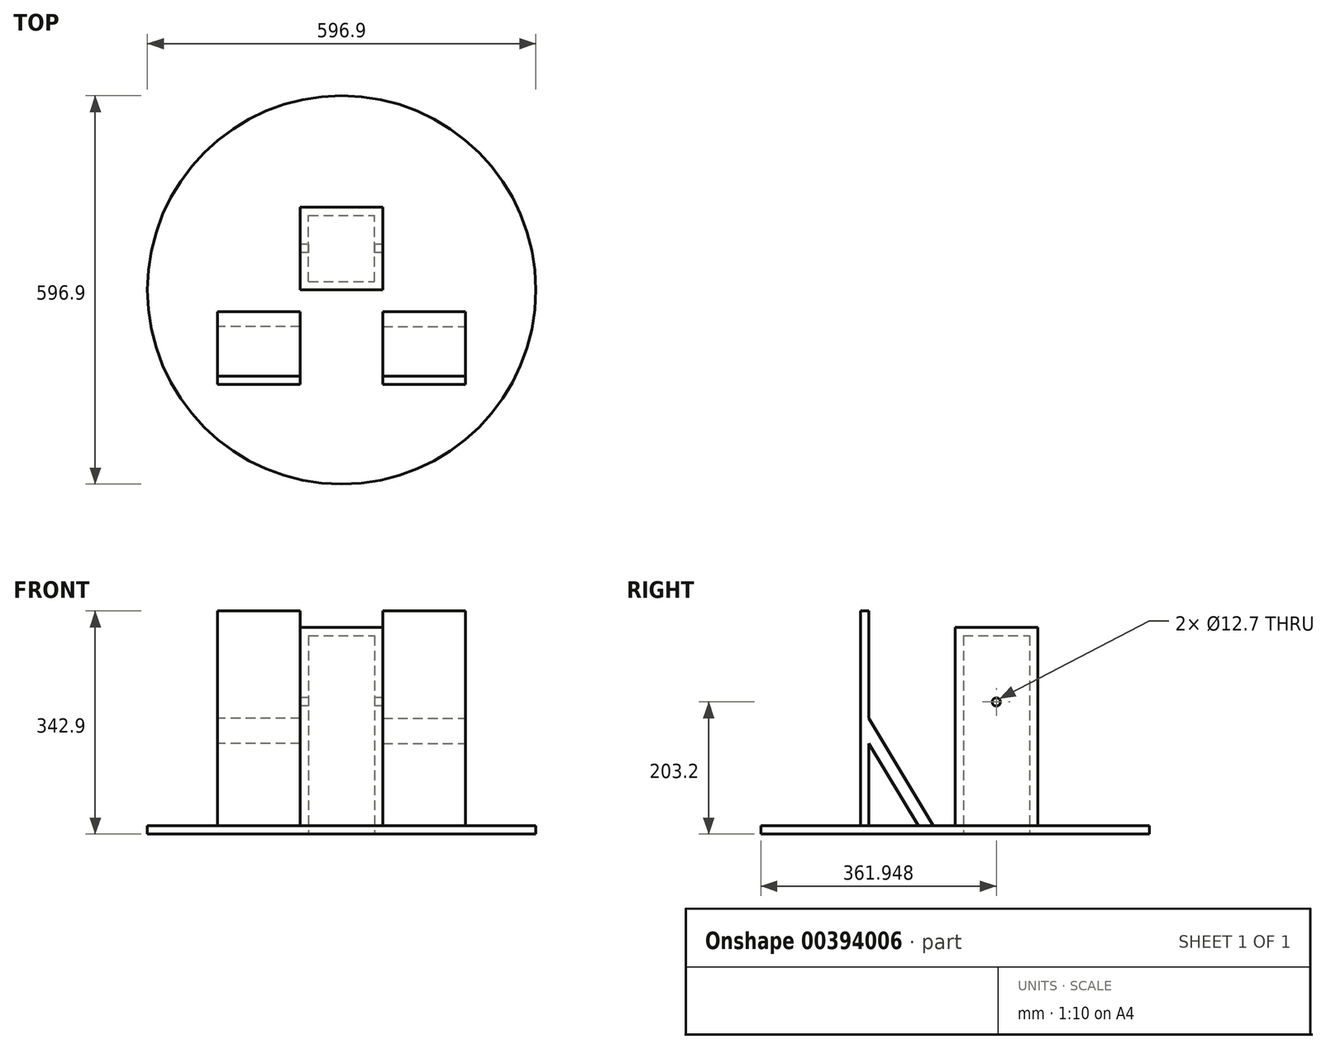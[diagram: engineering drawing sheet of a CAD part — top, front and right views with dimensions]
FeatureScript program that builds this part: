
annotation { "Feature Type Name" : "Feature", "Feature Type Description" : "" }
export const myFeature = defineFeature(function(context is Context, id is Id, definition is map)
    precondition{}
    {
        {
            var Q0;
            Q0=qCreatedBy(makeId("Top.planeOp"),FACE);
            var sketch = newSketch(context, id + "F0", { "sketchPlane" : qUnion([Q0])});
            skLineSegment(sketch, "E0.bottom", {"start": v(-59.76, 60.85) * mm, "end": v(67.24, 60.85) * mm});
            skLineSegment(sketch, "E0.top", {"start": v(-59.76, -66.15) * mm, "end": v(67.24, -66.15) * mm});
            skLineSegment(sketch, "E0.left", {"start": v(-59.76, 60.85) * mm, "end": v(-59.76, -66.15) * mm});
            skLineSegment(sketch, "E0.right", {"start": v(67.24, 60.85) * mm, "end": v(67.24, -66.15) * mm});
            skSolve(sketch);
        }
        {
            var Q0;
            Q0=qSketchRegion(id+"F0",true);
            extrude(context, id + "F1", {"entities" : qUnion([Q0]), "depth" : 304.8 * mm});
        }
        {
            var Q0;
            Q0=makeQuery(id+"F1.opExtrude","CAP_FACE",FACE,{"disambiguationData":[OSD([sQuery(id+"F0.wireOp",EDGE,"E0.bottom"),sQuery(id+"F0.wireOp",EDGE,"E0.top"),sQuery(id+"F0.wireOp",EDGE,"E0.left"),sQuery(id+"F0.wireOp",EDGE,"E0.right")])],"isStart":true});
            var sketch = newSketch(context, id + "F2", { "sketchPlane" : qUnion([Q0])});
            skLineSegment(sketch, "E1.0", {"start": v(-47.06, -60.85) * mm, "end": v(-47.06, 66.15) * mm, "construction": true});
            skLineSegment(sketch, "E2.0", {"start": v(-59.76, 53.45) * mm, "end": v(67.24, 53.45) * mm, "construction": true});
            skLineSegment(sketch, "E3.0", {"start": v(54.54, -60.85) * mm, "end": v(54.54, 66.15) * mm, "construction": true});
            skLineSegment(sketch, "E4.0", {"start": v(-59.76, -48.15) * mm, "end": v(67.24, -48.15) * mm, "construction": true});
            skLineSegment(sketch, "E5.bottom", {"start": v(-47.06, 53.45) * mm, "end": v(54.54, 53.45) * mm});
            skLineSegment(sketch, "E5.top", {"start": v(-47.06, -48.15) * mm, "end": v(54.54, -48.15) * mm});
            skLineSegment(sketch, "E5.left", {"start": v(-47.06, 53.45) * mm, "end": v(-47.06, -48.15) * mm});
            skLineSegment(sketch, "E5.right", {"start": v(54.54, 53.45) * mm, "end": v(54.54, -48.15) * mm});
            skSolve(sketch);
        }
        {
            var Q0;
            Q0=qSketchRegion(id+"F2",true);
            extrude(context, id + "F3", {"entities" : qUnion([Q0]), "operationType" : NewBodyOperationType.REMOVE, "oppositeDirection" : true, "depth" : 292.1 * mm});
        }
        {
            var Q0;
            Q0=makeQuery(id+"F1.opExtrude","SWEPT_FACE",FACE,{"disambiguationData":[OSD([sQuery(id+"F0.wireOp",EDGE,"E0.left")])]});
            var sketch = newSketch(context, id + "F4", { "sketchPlane" : qUnion([Q0])});
            skLineSegment(sketch, "E6.0", {"start": v(-60.85, 190.5) * mm, "end": v(66.15, 190.5) * mm, "construction": true});
            skCircle(sketch, "E7", {"center": v(2.65, 190.5) * mm, "radius": 6.35 * mm});
            skSolve(sketch);
        }
        {
            var Q0;
            Q0=qSketchRegion(id+"F4",true);
            extrude(context, id + "F5", {"entities" : qUnion([Q0]), "operationType" : NewBodyOperationType.REMOVE, "endBound" : BoundingType.THROUGH_ALL, "oppositeDirection" : true, "depth" : 25.4 * mm});
        }
        {
            var Q0;
            Q0=makeQuery(id+"F1.opExtrude","CAP_FACE",FACE,{"disambiguationData":[OSD([sQuery(id+"F0.wireOp",EDGE,"E0.bottom"),sQuery(id+"F0.wireOp",EDGE,"E0.top"),sQuery(id+"F0.wireOp",EDGE,"E0.left"),sQuery(id+"F0.wireOp",EDGE,"E0.right")])],"isStart":true});
            var sketch = newSketch(context, id + "F6", { "sketchPlane" : qUnion([Q0])});
            skCircle(sketch, "E8", {"center": v(3.74, 66.15) * mm, "radius": 298.45 * mm});
            skLineSegment(sketch, "E9", {"start": v(-47.06, 53.45) * mm, "end": v(-47.06, -48.15) * mm});
            skLineSegment(sketch, "E10", {"start": v(-47.06, -48.15) * mm, "end": v(54.54, -48.15) * mm});
            skLineSegment(sketch, "E11", {"start": v(54.54, -48.15) * mm, "end": v(54.54, 53.45) * mm});
            skLineSegment(sketch, "E12", {"start": v(54.54, 53.45) * mm, "end": v(-47.06, 53.45) * mm});
            skLineSegment(sketch, "E13", {"start": v(3.74, 66.15) * mm, "end": v(-294.7, 66.15) * mm});
            skLineSegment(sketch, "E14", {"start": v(3.74, 66.15) * mm, "end": v(302.2, 66.15) * mm});
            skSolve(sketch);
        }
        {
            var Q0;
            Q0=qSketchRegion(id+"F6",true);
            extrude(context, id + "F7", {"entities" : qUnion([Q0]), "operationType" : NewBodyOperationType.ADD, "depth" : 12.7 * mm});
        }
        {
            var Q0;
            Q0=makeQuery(id+"F7.opExtrude","CAP_FACE",FACE,{"disambiguationData":[OSD([sQuery(id+"F6.wireOp",EDGE,"E8"),sQuery(id+"F6.wireOp",EDGE,"E9"),sQuery(id+"F6.wireOp",EDGE,"E10"),sQuery(id+"F6.wireOp",EDGE,"E11"),sQuery(id+"F6.wireOp",EDGE,"E12")])],"isStart":true});
            var sketch = newSketch(context, id + "F8", { "sketchPlane" : qUnion([Q0])});
            skLineSegment(sketch, "E15.bottom", {"start": v(-59.76, -211.2) * mm, "end": v(-186.76, -211.2) * mm});
            skLineSegment(sketch, "E15.top", {"start": v(-59.76, -198.5) * mm, "end": v(-186.76, -198.5) * mm});
            skLineSegment(sketch, "E15.left", {"start": v(-59.76, -211.2) * mm, "end": v(-59.76, -198.5) * mm});
            skLineSegment(sketch, "E15.right", {"start": v(-186.76, -211.2) * mm, "end": v(-186.76, -198.5) * mm});
            skLineSegment(sketch, "E16.MirrorCS", {"start": v(67.24, -198.5) * mm, "end": v(194.24, -198.5) * mm});
            skLineSegment(sketch, "E17.MirrorCS", {"start": v(67.24, -211.2) * mm, "end": v(67.24, -198.5) * mm});
            skLineSegment(sketch, "E18.MirrorCS", {"start": v(194.24, -211.2) * mm, "end": v(194.24, -198.5) * mm});
            skLineSegment(sketch, "E19.MirrorCS", {"start": v(67.24, -211.2) * mm, "end": v(194.24, -211.2) * mm});
            skPoint(sketch, "E20.start.orphan", {"position": v(3.74, -66.15) * mm});
            skSolve(sketch);
        }
        {
            var Q0;
            Q0=qSketchRegion(id+"F8",true);
            extrude(context, id + "F9", {"entities" : qUnion([Q0]), "operationType" : NewBodyOperationType.ADD, "depth" : 330.2 * mm});
        }
        {
            var Q0;
            Q0=makeQuery(id+"F9.opExtrude","SWEPT_FACE",FACE,{"disambiguationData":[OSD([sQuery(id+"F8.wireOp",EDGE,"E18.MirrorCS")])]});
            var sketch = newSketch(context, id + "F10", { "sketchPlane" : qUnion([Q0])});
            skLineSegment(sketch, "E21", {"start": v(-198.5, 165.1) * mm, "end": v(-99.5, 0) * mm});
            skLineSegment(sketch, "E22", {"start": v(-99.5, 0) * mm, "end": v(-122.6, 0) * mm});
            skLineSegment(sketch, "E23", {"start": v(-122.6, 0) * mm, "end": v(-198.5, 126.6) * mm});
            skLineSegment(sketch, "E24", {"start": v(-198.5, 126.6) * mm, "end": v(-198.5, 165.1) * mm});
            skSolve(sketch);
        }
        {
            var Q0;
            Q0=qSketchRegion(id+"F10",true);
            extrude(context, id + "F11", {"entities" : qUnion([Q0]), "operationType" : NewBodyOperationType.ADD, "oppositeDirection" : true, "depth" : 127 * mm});
        }
        {
            var Q0;
            Q0=makeQuery(id+"F9.opExtrude","SWEPT_FACE",FACE,{"disambiguationData":[OSD([sQuery(id+"F8.wireOp",EDGE,"E15.right")])]});
            var sketch = newSketch(context, id + "F12", { "sketchPlane" : qUnion([Q0])});
            skLineSegment(sketch, "E25", {"start": v(198.5, 165.1) * mm, "end": v(99.5, 0) * mm});
            skLineSegment(sketch, "E26", {"start": v(99.5, 0) * mm, "end": v(122.6, 0) * mm});
            skLineSegment(sketch, "E27", {"start": v(122.6, 0) * mm, "end": v(198.5, 126.6) * mm});
            skLineSegment(sketch, "E28", {"start": v(198.5, 126.6) * mm, "end": v(198.5, 165.1) * mm});
            skSolve(sketch);
        }
        {
            var Q0;
            Q0=qSketchRegion(id+"F12",true);
            extrude(context, id + "F13", {"entities" : qUnion([Q0]), "operationType" : NewBodyOperationType.ADD, "oppositeDirection" : true, "depth" : 127 * mm});
        }
    });
